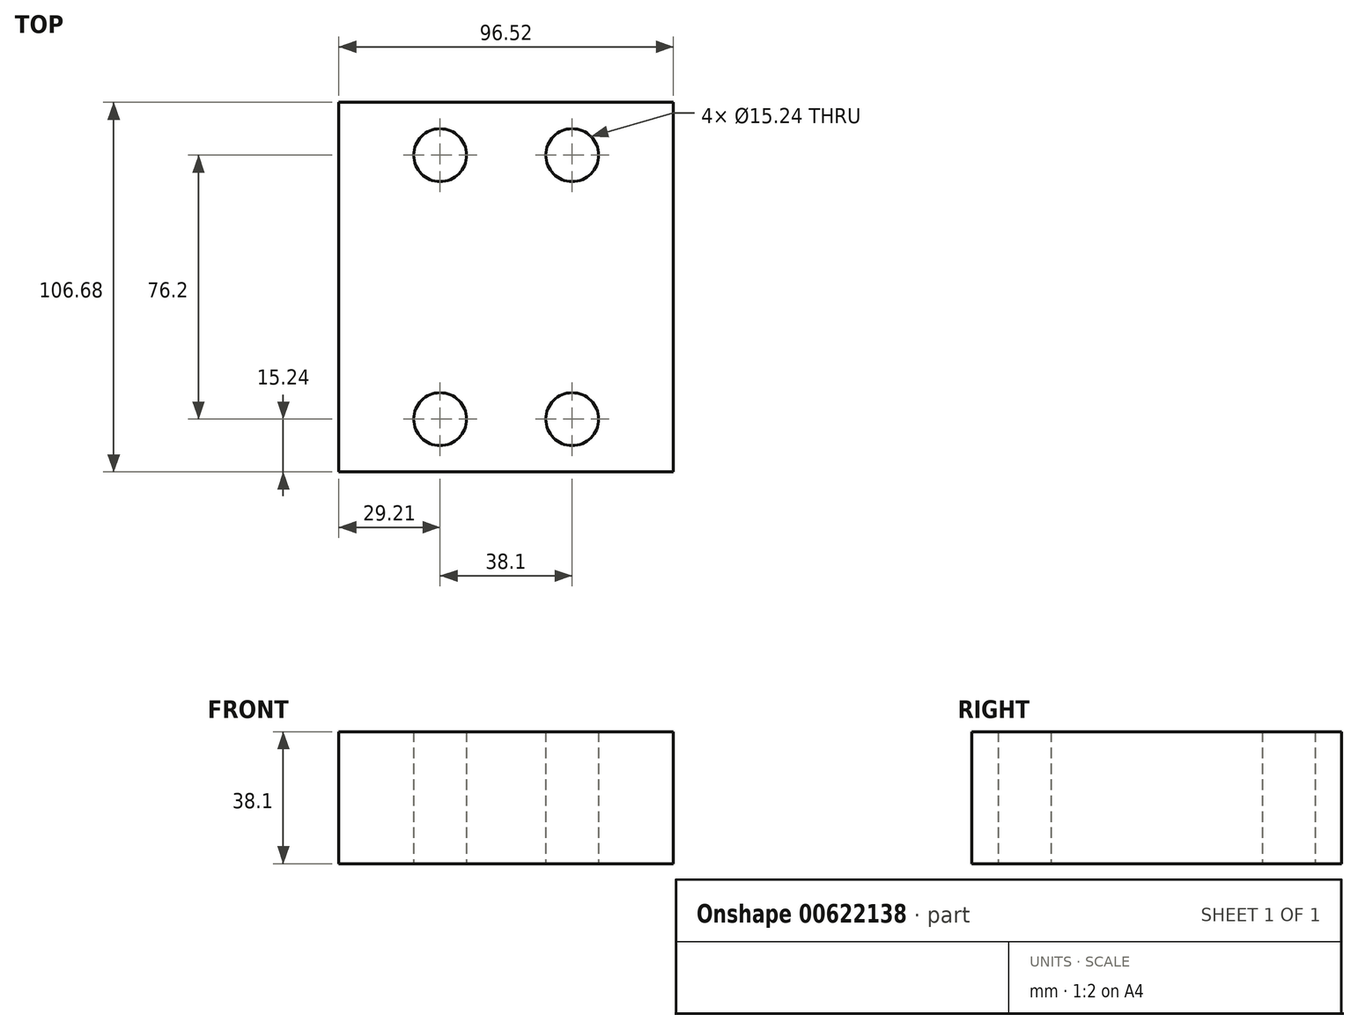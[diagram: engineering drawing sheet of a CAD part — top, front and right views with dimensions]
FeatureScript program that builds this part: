
annotation { "Feature Type Name" : "Feature", "Feature Type Description" : "" }
export const myFeature = defineFeature(function(context is Context, id is Id, definition is map)
    precondition{}
    {
        {
            var Q0;
            Q0=qCreatedBy(makeId("Top.planeOp"),FACE);
            var sketch = newSketch(context, id + "F0", { "sketchPlane" : qUnion([Q0])});
            skLineSegment(sketch, "E0.bottom", {"start": v(-48.26, 53.34) * mm, "end": v(48.26, 53.34) * mm});
            skLineSegment(sketch, "E0.top", {"start": v(-48.26, -53.34) * mm, "end": v(48.26, -53.34) * mm});
            skLineSegment(sketch, "E0.left", {"start": v(-48.26, 53.34) * mm, "end": v(-48.26, -53.34) * mm});
            skLineSegment(sketch, "E0.right", {"start": v(48.26, 53.34) * mm, "end": v(48.26, -53.34) * mm});
            skCircle(sketch, "E1", {"center": v(-19.05, 38.1) * mm, "radius": 7.62 * mm});
            skCircle(sketch, "E2", {"center": v(19.05, 38.1) * mm, "radius": 7.62 * mm});
            skCircle(sketch, "E3", {"center": v(19.05, -38.1) * mm, "radius": 7.62 * mm});
            skCircle(sketch, "E4", {"center": v(-19.05, -38.1) * mm, "radius": 7.62 * mm});
            skSolve(sketch);
        }
        {
            var Q0;
            Q0=makeQuery(id+"F0.imprint","IMPRINT",FACE,{"disambiguationData":[TD([[makeQuery(id+"F0.imprint","IMPRINT",EDGE,{"derivedFrom":sQuery(id+"F0.wireOp",EDGE,"E0.bottom")}),-1.0]])]});
            extrude(context, id + "F1", {"entities" : qUnion([Q0]), "depth" : 38.1 * mm, "offsetDistance" : 25.4 * mm});
        }
    });
